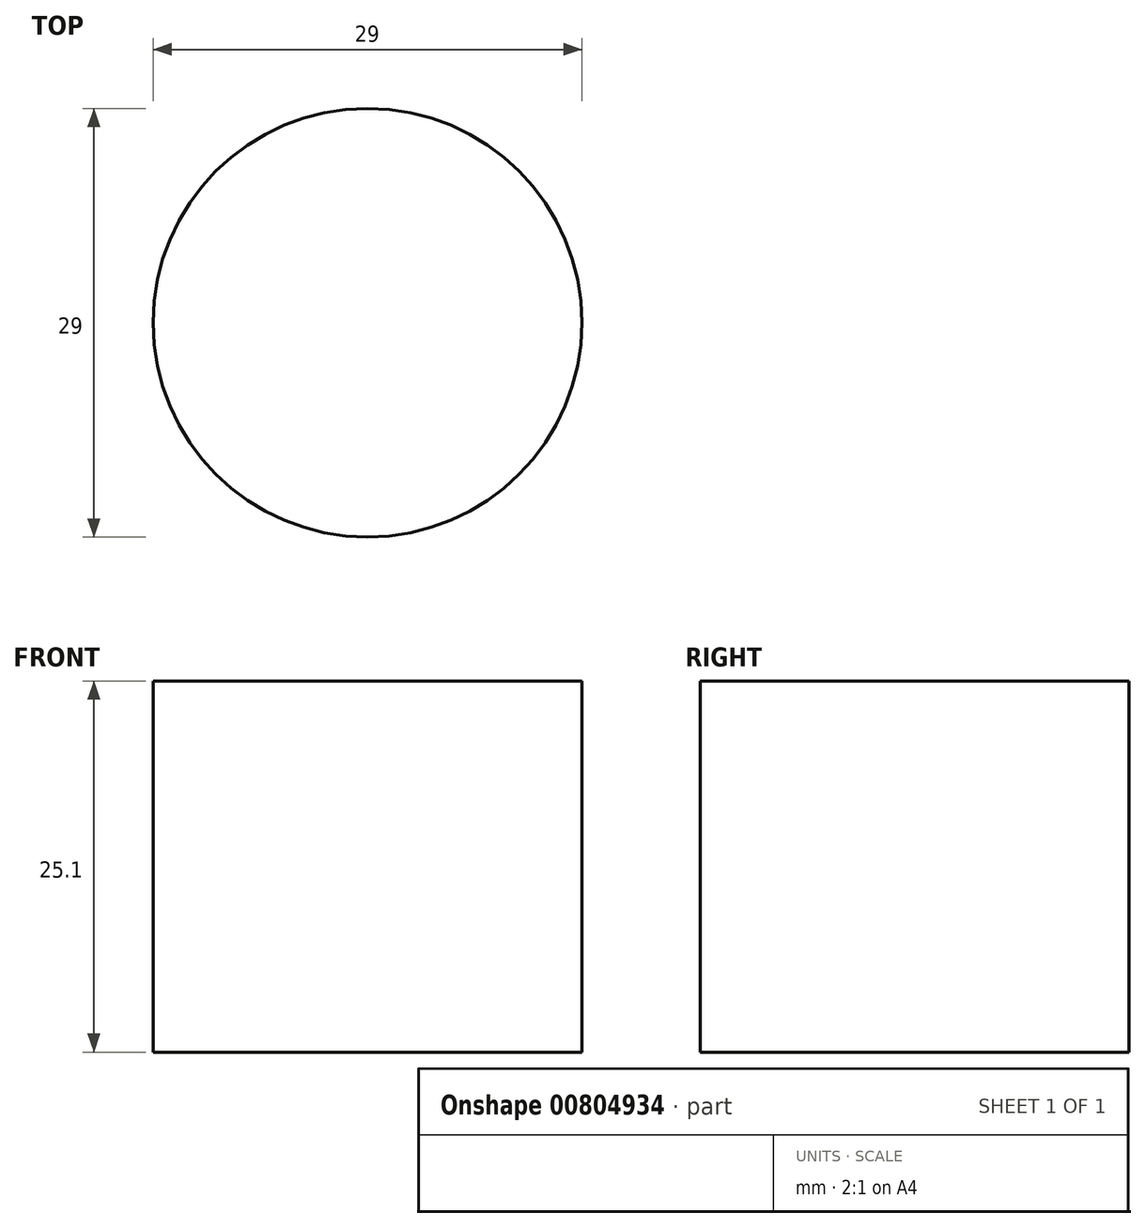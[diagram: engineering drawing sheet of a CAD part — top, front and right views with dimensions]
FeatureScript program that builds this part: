
annotation { "Feature Type Name" : "Feature", "Feature Type Description" : "" }
export const myFeature = defineFeature(function(context is Context, id is Id, definition is map)
    precondition{}
    {
        {
            var Q0;
            Q0=qCreatedBy(makeId("Top.planeOp"),FACE);
            var sketch = newSketch(context, id + "F0", { "sketchPlane" : qUnion([Q0])});
            skCircle(sketch, "E0", {"center": v(0, 0) * mm, "radius": 14.5 * mm});
            skSolve(sketch);
        }
        {
            var Q0;
            Q0 = qSketchRegion(id + "F0", true);
            extrude(context, id + "F1", {"entities" : qUnion([Q0]), "depth" : 25.1 * mm, "offsetDistance" : 25.4 * mm});
        }
    });
